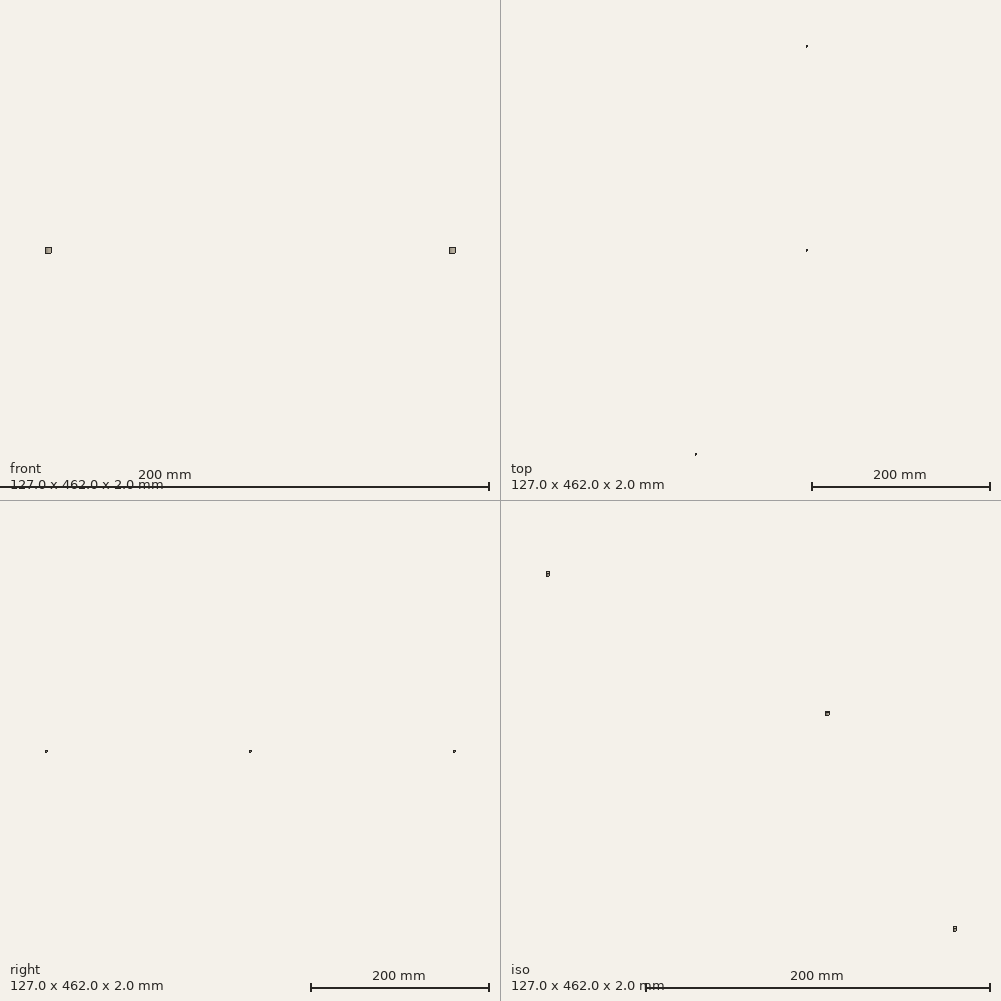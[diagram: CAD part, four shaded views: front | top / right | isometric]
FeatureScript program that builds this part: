
annotation { "Feature Type Name" : "Feature", "Feature Type Description" : "" }
export const myFeature = defineFeature(function(context is Context, id is Id, definition is map)
    precondition{}
    {
        {
            var Q0;
            Q0=qCreatedBy(makeId("Top.planeOp"),FACE);
            var sketch = newSketch(context, id + "F0", { "sketchPlane" : qUnion([Q0])});
            skLineSegment(sketch, "E0.bottom", {"start": v(77.5, -240) * mm, "end": v(-77.5, -240) * mm});
            skLineSegment(sketch, "E0.top", {"start": v(77.5, 240) * mm, "end": v(-77.5, 240) * mm});
            skLineSegment(sketch, "E0.left", {"start": v(77.5, -240) * mm, "end": v(77.5, 240) * mm});
            skLineSegment(sketch, "E0.right", {"start": v(-77.5, -240) * mm, "end": v(-77.5, 240) * mm});
            skPoint(sketch, "E0.middle", {"position": v(0, 0) * mm});
            skSolve(sketch);
        }
        {
            var Q0;
            Q0=makeQuery(id+"F0.imprint","IMPRINT",FACE,{"disambiguationData":[TD([[makeQuery(id+"F0.imprint","IMPRINT",EDGE,{"derivedFrom":sQuery(id+"F0.wireOp",EDGE,"E0.bottom")}),-1.0]])]});
            extrude(context, id + "F1", {"entities" : qUnion([Q0]), "depth" : 2 * mm});
        }
        {
            var Q0;
            Q0=makeQuery(id+"F1.opExtrude","CAP_FACE",FACE,{"disambiguationData":[OSD([sQuery(id+"F0.wireOp",EDGE,"E0.bottom"),sQuery(id+"F0.wireOp",EDGE,"E0.top"),sQuery(id+"F0.wireOp",EDGE,"E0.left"),sQuery(id+"F0.wireOp",EDGE,"E0.right")])],"isStart":false});
            var sketch = newSketch(context, id + "F2", { "sketchPlane" : qUnion([Q0])});
            skCircle(sketch, "E1", {"center": v(-62.5, 230) * mm, "radius": 1 * mm});
            skCircle(sketch, "E2.MirrorC", {"center": v(62.5, 230) * mm, "radius": 1 * mm});
            skCircle(sketch, "E3.MirrorC", {"center": v(-62.5, -230) * mm, "radius": 1 * mm});
            skCircle(sketch, "E4.MirrorC", {"center": v(62.5, -230) * mm, "radius": 1 * mm});
            skCircle(sketch, "E5", {"center": v(-62.5, 0) * mm, "radius": 1 * mm});
            skCircle(sketch, "E6.MirrorC", {"center": v(62.5, 0) * mm, "radius": 1 * mm});
            skCircle(sketch, "E7", {"center": v(0, 0) * mm, "radius": 1 * mm});
            skSolve(sketch);
        }
        {
            var Q0;
            Q0=makeQuery(id+"F2.imprint","IMPRINT",FACE,{"disambiguationData":[TD([[makeQuery(id+"F2.imprint","IMPRINT",EDGE,{"derivedFrom":sQuery(id+"F2.wireOp",EDGE,"E1")}),1.0]])]});
            var Q1;
            Q1=makeQuery(id+"F2.imprint","IMPRINT",FACE,{"disambiguationData":[TD([[makeQuery(id+"F2.imprint","IMPRINT",EDGE,{"derivedFrom":sQuery(id+"F2.wireOp",EDGE,"E2.MirrorC")}),-1.0]])]});
            var Q2;
            Q2=makeQuery(id+"F2.imprint","IMPRINT",FACE,{"disambiguationData":[TD([[makeQuery(id+"F2.imprint","IMPRINT",EDGE,{"derivedFrom":sQuery(id+"F2.wireOp",EDGE,"E3.MirrorC")}),-1.0]])]});
            var Q3;
            Q3=makeQuery(id+"F2.imprint","IMPRINT",FACE,{"disambiguationData":[TD([[makeQuery(id+"F2.imprint","IMPRINT",EDGE,{"derivedFrom":sQuery(id+"F2.wireOp",EDGE,"E4.MirrorC")}),1.0]])]});
            var Q4;
            Q4=makeQuery(id+"F2.imprint","IMPRINT",FACE,{"disambiguationData":[TD([[makeQuery(id+"F2.imprint","IMPRINT",EDGE,{"derivedFrom":sQuery(id+"F2.wireOp",EDGE,"E5")}),1.0]])]});
            var Q5;
            Q5=makeQuery(id+"F2.imprint","IMPRINT",FACE,{"disambiguationData":[TD([[makeQuery(id+"F2.imprint","IMPRINT",EDGE,{"derivedFrom":sQuery(id+"F2.wireOp",EDGE,"E6.MirrorC")}),-1.0]])]});
            var Q6;
            Q6=makeQuery(id+"F2.imprint","IMPRINT",FACE,{"disambiguationData":[TD([[makeQuery(id+"F2.imprint","IMPRINT",EDGE,{"derivedFrom":sQuery(id+"F2.wireOp",EDGE,"E7")}),1.0]])]});
            extrude(context, id + "F3", {"entities" : qUnion([Q0, Q1, Q2, Q3, Q4, Q5, Q6]), "operationType" : NewBodyOperationType.REMOVE, "oppositeDirection" : true, "depth" : 25 * mm});
        }
    });
